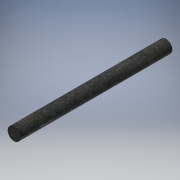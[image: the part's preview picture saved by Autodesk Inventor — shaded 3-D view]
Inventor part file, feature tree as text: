
AUTODESK INVENTOR PART (.ipt)
format: ipt  version: 2016 (Build 200138000, 138)  size: 93,696 bytes
history: native  units: in
note: dims shown in document units (in); Inventor stores cm internally (conversion verified against a paired STEP export)
features: extrude x1, sketch x1
ambient origin geometry x8: Origin, YZ Plane, XZ Plane, XY Plane, X Axis, Y Axis, Z Axis, Center Point
bodies: Solid1 (feature_tree)
feature tree (2):
  extrude  "Extrusion1"  Depth=3.0in TaperAngle=0.0deg
  sketch  "Sketch1"  dims[d0=0.25in d1=3.0in d2=0.0in]
